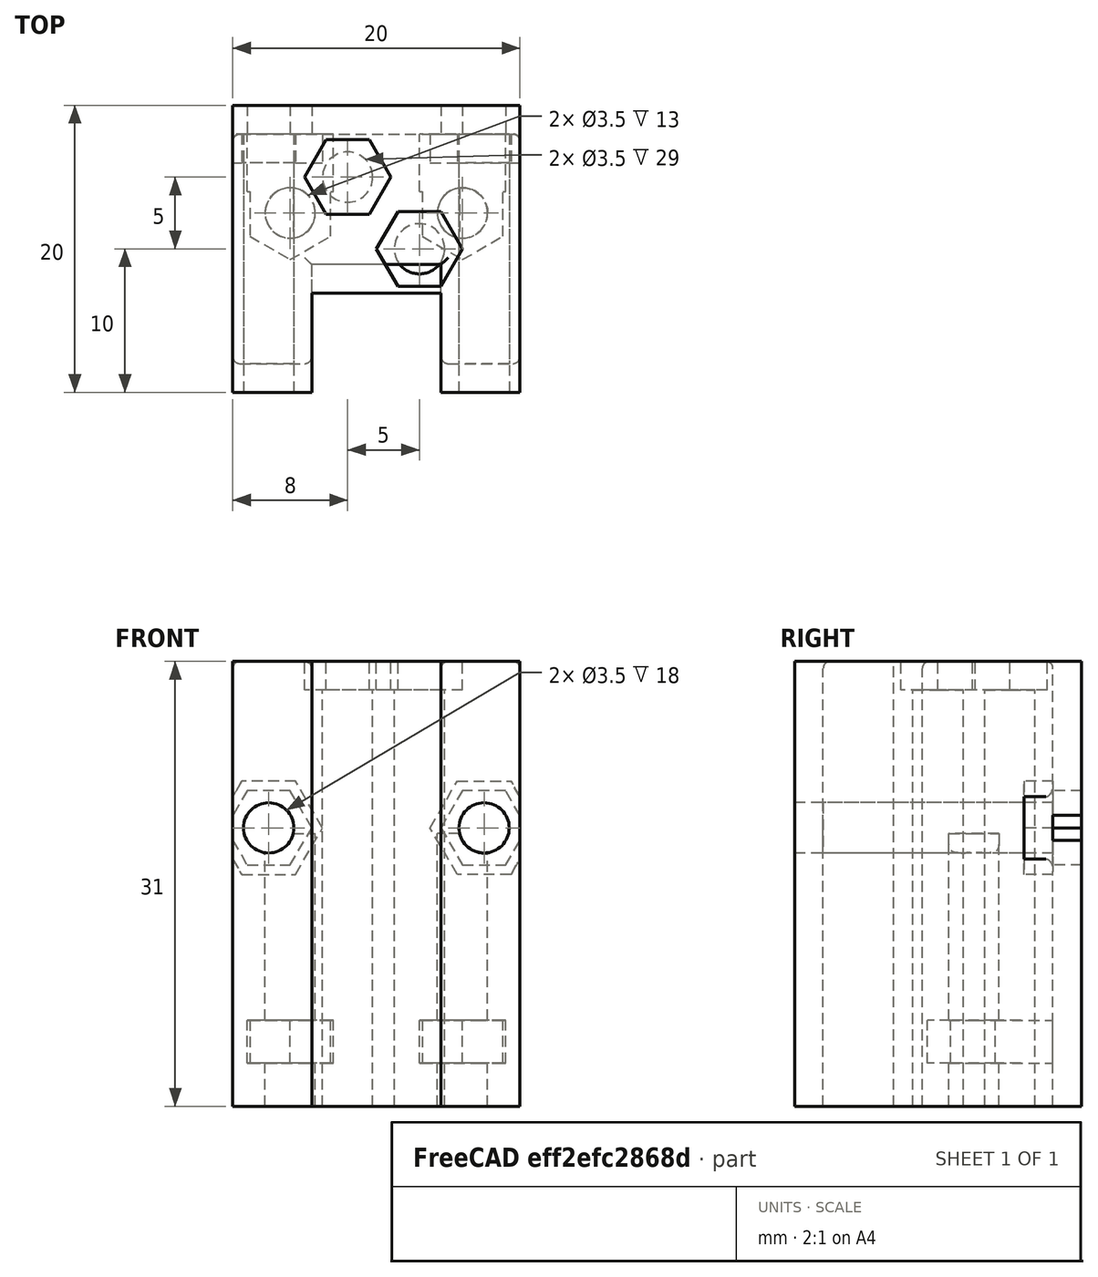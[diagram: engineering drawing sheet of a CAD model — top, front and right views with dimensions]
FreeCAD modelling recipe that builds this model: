
FCSTD DOCUMENT  (FreeCAD 0.19R14555 (Git shallow))
Label: Soporte sensor vueltas
License: All rights reserved
LicenseURL: http://en.wikipedia.org/wiki/All_rights_reserved
objects: Part::Cut×18, Part::Prism×8, Part::Box×8, Part::Cylinder×8, Part::MultiFuse×2, Part::Fillet×2
note: 46 computed .brp shape members not serialized (recipe doc carries the construction recipe); baked Part::Feature solids carry a one-line shape summary decoded from their .brp

FEATURE [Part::Prism] Prism  label="Prisma"
  AttacherType = Attacher::AttachEngine3D
  Circumradius = 3
  FirstAngle = 0
  Height = 10
  Placement = pos=(2.5,28,19.4) rot=(1,0,0;1.5708rad)
  Polygon = 6
  SecondAngle = 0
FEATURE [Part::Box] Box  label="Cubo"
  AttacherType = Attacher::AttachEngine3D
  Height = 31
  Length = 20
  Width = 20
FEATURE [Part::Cut] Cut
  Base = -> Box
  Tool = -> Prism
FEATURE [Part::Prism] Prism001  label="Prisma001"
  AttacherType = Attacher::AttachEngine3D
  Circumradius = 3
  FirstAngle = 0
  Height = 10
  Placement = pos=(17.5,28,19.4) rot=(1,0,0;1.5708rad)
  Polygon = 6
  SecondAngle = 0
FEATURE [Part::Cut] Cut001
  Base = -> Cut
  Tool = -> Prism001
FEATURE [Part::Cylinder] Cylinder001  label="Cilindro001"
  Angle = 360
  AttacherType = Attacher::AttachEngine3D
  Height = 41
  Placement = pos=(2.5,30,19.4) rot=(1,0,0;1.5708rad)
  Radius = 1.75
FEATURE [Part::Cylinder] Cylinder002  label="Cilindro002"
  Angle = 360
  AttacherType = Attacher::AttachEngine3D
  Height = 39
  Placement = pos=(17.5,32,19.4) rot=(1,0,0;1.5708rad)
  Radius = 1.75
FEATURE [Part::Cut] Cut002
  Base = -> Cut001
  Tool = -> Cylinder001
FEATURE [Part::Cut] Cut003
  Base = -> Cut002
  Tool = -> Cylinder002
FEATURE [Part::Cylinder] Cylinder003  label="Cilindro003"
  Angle = 360
  AttacherType = Attacher::AttachEngine3D
  Height = 40
  Placement = pos=(13,10,-3) rot=(0,0,1;0rad)
  Radius = 1.75
FEATURE [Part::Cylinder] Cylinder004  label="Cilindro004"
  Angle = 360
  AttacherType = Attacher::AttachEngine3D
  Height = 43
  Placement = pos=(8,15,-3) rot=(0,0,1;0rad)
  Radius = 1.75
FEATURE [Part::Cut] Cut004
  Base = -> Cut003
  Tool = -> Cylinder003
FEATURE [Part::Cut] Cut005
  Base = -> Cut004
  Tool = -> Cylinder004
FEATURE [Part::Prism] Prism002  label="Prisma002"
  AttacherType = Attacher::AttachEngine3D
  Circumradius = 3
  FirstAngle = 0
  Height = 10
  Placement = pos=(13,10,29) rot=(0,0,1;0rad)
  Polygon = 6
  SecondAngle = 0
FEATURE [Part::Prism] Prism003  label="Prisma003"
  AttacherType = Attacher::AttachEngine3D
  Circumradius = 3
  FirstAngle = 0
  Height = 10
  Placement = pos=(8,15,29) rot=(0,0,1;0rad)
  Polygon = 6
  SecondAngle = 0
FEATURE [Part::Cut] Cut006
  Base = -> Cut005
  Tool = -> Prism002
FEATURE [Part::Cut] Cut007
  Base = -> Cut006
  Tool = -> Prism003
FEATURE [Part::Box] Box001  label="Cubo001"
  AttacherType = Attacher::AttachEngine3D
  Height = 42
  Length = 9
  Placement = pos=(5.5,-0.1,-6) rot=(0,0,1;0rad)
  Width = 7
FEATURE [Part::Cut] Cut008  label="Nada"
  Base = -> Cut007
  Tool = -> Box001
FEATURE [Part::Cylinder] Cylinder005  label="Cilindro005"
  Angle = 360
  AttacherType = Attacher::AttachEngine3D
  Height = 20
  Placement = pos=(34,7.5,-1) rot=(0,0,1;0rad)
  Radius = 1.75
FEATURE [Part::Prism] Prism004  label="Prisma004"
  AttacherType = Attacher::AttachEngine3D
  Circumradius = 3.25
  FirstAngle = 0
  Height = 3
  Placement = pos=(34,7.5,3) rot=(0,0,1;1.5708rad)
  Polygon = 6
  SecondAngle = 0
FEATURE [Part::Box] Box004  label="Cubo004"
  AttacherType = Attacher::AttachEngine3D
  Height = 3
  Length = 6
  Placement = pos=(31,9,3) rot=(0,0,1;0rad)
  Width = 20
FEATURE [Part::MultiFuse] Fusion001
  Placement = pos=(-18,5,0) rot=(0,1,0;0rad)
  Shapes = -> [Box004,Prism004,Cylinder005]
FEATURE [Part::Box] Box005  label="Cubo005"
  AttacherType = Attacher::AttachEngine3D
  Height = 31
  Length = 20
  Width = 20
FEATURE [Part::Cylinder] Cylinder006  label="Cilindro006"
  Angle = 360
  AttacherType = Attacher::AttachEngine3D
  Height = 39
  Placement = pos=(17.5,32,19.4) rot=(1,0,0;1.5708rad)
  Radius = 1.75
FEATURE [Part::Prism] Prism005  label="Prisma005"
  AttacherType = Attacher::AttachEngine3D
  Circumradius = 3.75
  FirstAngle = 0
  Height = 10
  Placement = pos=(17.5,26,19.4) rot=(1,0,0;1.5708rad)
  Polygon = 6
  SecondAngle = 0
FEATURE [Part::Cylinder] Cylinder007  label="Cilindro007"
  Angle = 360
  AttacherType = Attacher::AttachEngine3D
  Height = 41
  Placement = pos=(2.5,30,19.4) rot=(1,0,0;1.5708rad)
  Radius = 1.75
FEATURE [Part::Prism] Prism006  label="Prisma006"
  AttacherType = Attacher::AttachEngine3D
  Circumradius = 3.75
  FirstAngle = 0
  Height = 10
  Placement = pos=(2.5,26,19.4) rot=(1,0,0;1.5708rad)
  Polygon = 6
  SecondAngle = 0
FEATURE [Part::Cut] Cut009
  Base = -> Box005
  Tool = -> Prism006
FEATURE [Part::Cut] Cut010
  Base = -> Cut009
  Tool = -> Prism005
FEATURE [Part::Cut] Cut011
  Base = -> Cut010
  Tool = -> Cylinder007
FEATURE [Part::Cut] Cut012
  Base = -> Cut011
  Tool = -> Cylinder006
FEATURE [Part::Box] Box006  label="Cubo006"
  AttacherType = Attacher::AttachEngine3D
  Height = 42
  Length = 9
  Placement = pos=(5.5,-0.1,-6) rot=(0,0,1;0rad)
  Width = 9
FEATURE [Part::Cut] Cut013
  Base = -> Cut012
  Tool = -> Box006
FEATURE [Part::Cylinder] Cylinder008  label="Cilindro008"
  Angle = 360
  AttacherType = Attacher::AttachEngine3D
  Height = 20
  Placement = pos=(34,7.5,-1) rot=(0,0,1;0rad)
  Radius = 1.75
FEATURE [Part::Prism] Prism007  label="Prisma007"
  AttacherType = Attacher::AttachEngine3D
  Circumradius = 3.25
  FirstAngle = 0
  Height = 3
  Placement = pos=(34,7.5,3) rot=(0,0,1;1.5708rad)
  Polygon = 6
  SecondAngle = 0
FEATURE [Part::Box] Box007  label="Cubo007"
  AttacherType = Attacher::AttachEngine3D
  Height = 3
  Length = 6
  Placement = pos=(31,9,3) rot=(0,0,1;0rad)
  Width = 20
FEATURE [Part::MultiFuse] Fusion002
  Placement = pos=(-30,5,0) rot=(0,1,0;0rad)
  Shapes = -> [Box007,Prism007,Cylinder008]
FEATURE [Part::Cut] Cut014
  Base = -> Cut013
  Tool = -> Fusion002
FEATURE [Part::Cut] Cut015
  Base = -> Cut014
  Tool = -> Fusion001
FEATURE [Part::Fillet] Fillet
  Base = -> Cut015
  Edges = 16 edges r=0.5: [Edge1,Edge2,Edge6,Edge8,Edge9,Edge10,Edge11,Edge12,Edge13,Edge14,Edge15,Edge16,Edge29,Edge56,Edge61,Edge62]
FEATURE [Part::Box] Box008  label="Cubo008"
  AttacherType = Attacher::AttachEngine3D
  Height = 35
  Length = 30
  Placement = pos=(0,18,0) rot=(0,0,1;0rad)
  Width = 30
FEATURE [Part::Box] Box009  label="Cubo009"
  AttacherType = Attacher::AttachEngine3D
  Height = 35
  Length = 30
  Placement = pos=(0,-28,0) rot=(0,0,1;0rad)
  Width = 30
FEATURE [Part::Cut] Cut016
  Base = -> Fillet
  Tool = -> Box008
FEATURE [Part::Cut] Cut017
  Base = -> Cut016
  Tool = -> Box009
FEATURE [Part::Fillet] Fillet001
  Base = -> Cut017
  Edges = 11 edges r=0.5: [Edge3,Edge5,Edge7,Edge19,Edge26,Edge28,Edge51,Edge53,Edge66,Edge82,Edge123]
